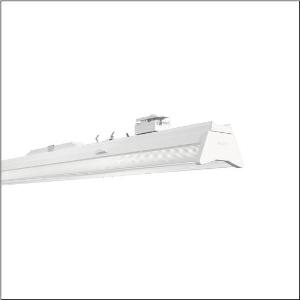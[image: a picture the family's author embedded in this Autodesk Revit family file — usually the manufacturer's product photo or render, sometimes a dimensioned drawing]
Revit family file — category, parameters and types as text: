
# Revit family: licross_r__21_performance_mo_52td16dn445g_3218
name_source: partatom
category: Lighting Fixtures
units: mm (PartAtom-declared; Revit-internal decimal feet)

## family parameters
Cut with Voids When Loaded = No
Host = Face
Light Source = No
Part Type = Normal
Room Calculation Point = No
Round Connector Dimension = Use Diameter
Shared = No

## types (1)
- --- (1 x LED, 4500 lm, 24.9 W, 4000K)
    Apparent Load = 25 VA
    CIE Flux Codes = 66 88 96 79 100
    Color Rendering = 80
    Color Temperature = 4000K
    Default Elevation = 1800 mm
    Description = Licross® 21 Performance MO, luminaire insert, of sheet steel, galvanised, coil coated, white, length: 1.500mm, width: 120mm, height: 123mm, LED rated luminous flux: 4.500lm, light colour: 840, control gear: DALI 2, with plug, 5-pole, with phase selection, mains connection: 220..240V, AC, 50/60Hz, rated input power: 25W, halogen-free wiring, primary light control with lens, of plastic, primary optical cover: cover, of PMMA, CAT 2 (L<= 3000cd/m²), light emission: direct/indirect distribution, primary light characteristic: symmetric, protection rating (complete): IP54, insulation class (complete): insulation class I (protective earthing), certification: CE, ENEC, VDE, UKCA, protection symbol: D if used in an environment with non-conductive dust loads with corresponding accessories, impact resistance: IK06, permissible ambient temperature for indoor applications: -25..+50°C, corresponds to IFS (International Featured Standards) requirements for safety and quality in the food industry, reducing of maximum allowable ambient temperature of 5°C with ceiling mounting, LABS conformity tested according to VDMA 24364:2018-05, packaging unit: 1 piece
    Height = 114 mm
    Lamp = 1 x LED
    Lamp Light Flux = 4500 lm
    Lamp Power = 24.9 W
    Lamp count = 1
    Length = 1500 mm
    Luminous efficacy = 181 lm/W
    Manufacturer = Siteco
    ModVariant = No
    Model = 52TD16DN445G
    Mounting Place = Ceiling
    Mounting Type = Pendant
    Number of Poles = 1
    OnlyDefault = Yes
    Power Factor = 1
    Product Name = Licross® 21 Performance MO
    Product group = luminaire insert
    ProductGroupID = 901
    Protection Class = Protection class I
    Protection Degree = IP 54
    RLX_Detail_Level = 1
    RLX_Emergency_Light_Flux = 0 lm
    RLX_Emergency_Type = 0
    RLX_Emergency_Type_DB = No
    RlxData = <blob elided: 33541 chars, md5=0f7b49e6>
    Socket = socket
    Standby Power = 0 W
    System Light Flux = 4500 lm
    System Power = 25 W
    Type Comments = factory setting: luminous flux: 100 % | dim-lin: 254 | 165 mA
    Type Image = l_1256138.jpg
    URL = http://relux.com
    VarID = @adj_006931
    Voltage = 0 V
    Weight = 0.00 kg
    Width = 120 mm

## geometry (parser evidence)
native form markers: Blend x4, Sweep x12
no freeform markers — native parametric forms only
